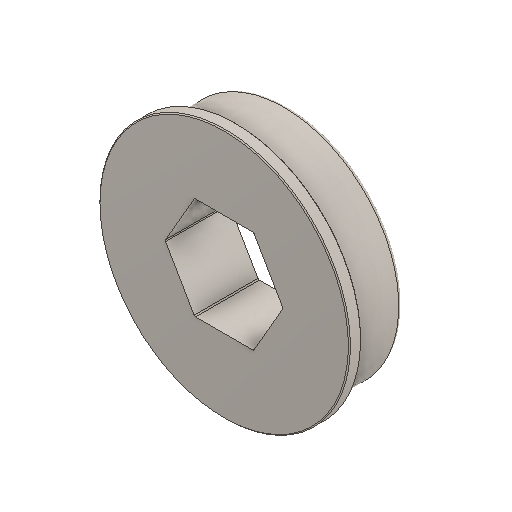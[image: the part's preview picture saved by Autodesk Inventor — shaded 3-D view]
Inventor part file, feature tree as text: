
AUTODESK INVENTOR PART (.ipt)
format: ipt  version: 2024.1 (Build 281209000, 209)  size: 165,888 bytes
history: native  units: in
note: dims shown in document units (in); Inventor stores cm internally (conversion verified against a paired STEP export)
features: fillet x1
ambient origin geometry x8: Origin, YZ Plane, XZ Plane, XY Plane, X Axis, Y Axis, Z Axis, Center Point
bodies: Solid1 (feature_tree)
feature tree (1):
  fillet  "Fillet2"  [1 undecoded]
note: 1 required parameter value undecoded (feature->parameter linkage not recoverable at this tier; creation-order binding heuristic only, values carry confidence <= 0.55)
